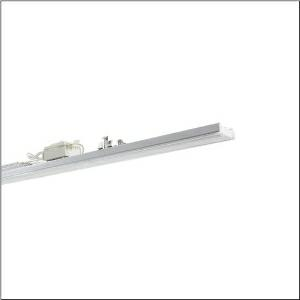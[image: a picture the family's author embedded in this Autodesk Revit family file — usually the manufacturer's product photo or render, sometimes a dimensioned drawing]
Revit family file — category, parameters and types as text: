
# Revit family: licross_r__21_recessed_ho_52tl12dv4l2md_9758
name_source: partatom
category: Lighting Fixtures
units: mm (PartAtom-declared; Revit-internal decimal feet)

## family parameters
Cut with Voids When Loaded = No
Host = Face
Light Source = No
Part Type = Normal
Room Calculation Point = No
Round Connector Dimension = Use Diameter
Shared = No

## types (1)
- --- (1 x LED, 22710 lm, 125.6 W, 4000K)
    Apparent Load = 126 VA
    CIE Flux Codes = 69 91 98 100 100
    Color Rendering = 80
    Color Temperature = 4000K
    Default Elevation = 1800 mm
    Description = Licross® 21 Recessed HO, luminaire insert, of sheet steel, galvanised, coil coated, white, length: 2.250mm, width: 66mm, height: 67mm, LED rated luminous flux: 22.710lm, light colour: 840, control gear: DALI 2 (for two DALI lines), with plug, 6-pole, with phase selection, mains connection: 220..240V, AC/DC, 0/50..60Hz, rated input power: 126W, without changeover relay, for emergency light function, for central battery installations according to DIN EN 60598-2-22, halogen-free wiring, primary optical cover: cover, of PMMA, light emission: direct distribution, primary light characteristic: symmetric, protection rating (complete): IP40, insulation class (complete): insulation class I (protective earthing), certification: CE, ENEC, VDE, UKCA, protection symbol: D if used in an environment without relevant dust loads with corresponding accessories, impact resistance: IK06, permissible ambient temperature for indoor applications: -40..+30°C, standard: EN 60598-2-22, corresponds to IFS (International Featured Standards) requirements for safety and quality in the food industry, reducing of maximum allowable ambient temperature of 5°C with ceiling mounting, LABS conformity tested according to VDMA 24364:2018-05, packaging unit: 1 piece
    Height = 58 mm
    Lamp = 1 x LED
    Lamp Light Flux = 22710 lm
    Lamp Power = 125.6 W
    Lamp count = 1
    Length = 2250 mm
    Luminous efficacy = 181 lm/W
    Manufacturer = Siteco
    ModVariant = No
    Model = 52TL12DV4L2MD
    Mounting Place = Ceiling
    Mounting Type = Pendant
    Number of Poles = 1
    OnlyDefault = Yes
    Power Factor = 1
    Product Name = Licross® 21 Recessed HO
    Product group = luminaire insert
    ProductGroupID = 902
    Protection Class = Protection class I
    Protection Degree = IP 40
    RLX_Detail_Level = 1
    RLX_Emergency_Light_Flux = 0 lm
    RLX_Emergency_Type = 0
    RLX_Emergency_Type_DB = No
    RlxData = <blob elided: 30073 chars, md5=ed69c0d6>
    Socket = socket
    Standby Power = 0 W
    System Light Flux = 22710 lm
    System Power = 126 W
    Type Comments = : AC-mode, luminous flux: 100 % | dim-lin: 254 | 489 mA
    Type Image = l_1296930.jpg
    URL = http://relux.com
    VarID = @adj_111724
    Voltage = 0 V
    Weight = 0.00 kg
    Width = 66 mm

## geometry (parser evidence)
native form markers: Blend x4, Sweep x9
no freeform markers — native parametric forms only
